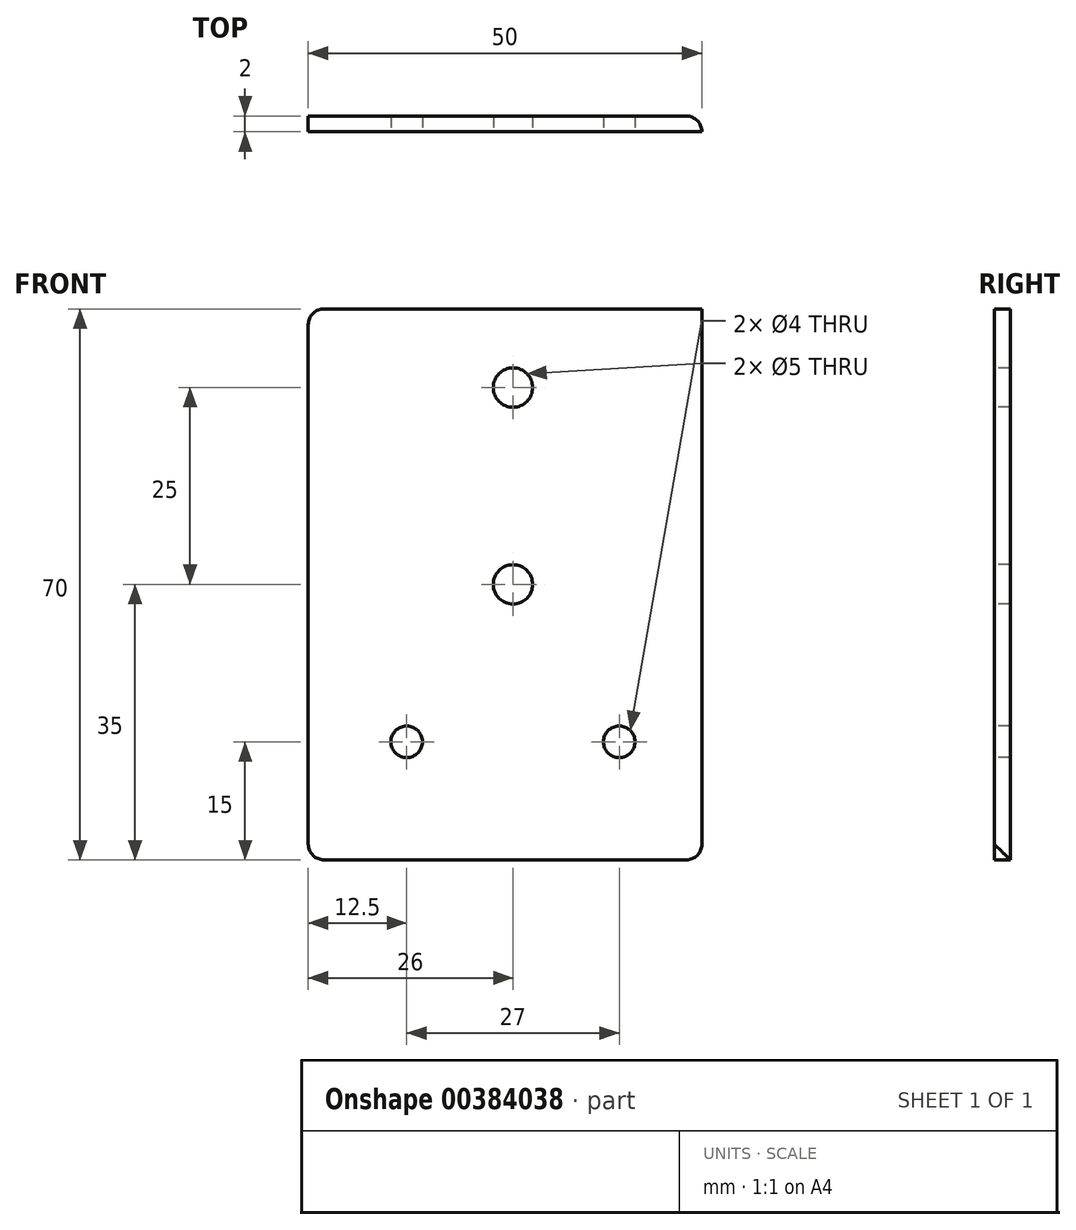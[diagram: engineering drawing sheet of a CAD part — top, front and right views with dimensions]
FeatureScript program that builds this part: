
annotation { "Feature Type Name" : "Feature", "Feature Type Description" : "" }
export const myFeature = defineFeature(function(context is Context, id is Id, definition is map)
    precondition{}
    {
        {
            var Q0;
            Q0=qCreatedBy(makeId("Front.planeOp"),FACE);
            var sketch = newSketch(context, id + "F0", { "sketchPlane" : qUnion([Q0])});
            skLineSegment(sketch, "E0.bottom", {"start": v(0, 0) * mm, "end": v(50, 0) * mm});
            skLineSegment(sketch, "E0.top", {"start": v(0, 70) * mm, "end": v(50, 70) * mm});
            skLineSegment(sketch, "E0.left", {"start": v(0, 0) * mm, "end": v(0, 70) * mm});
            skLineSegment(sketch, "E0.right", {"start": v(50, 0) * mm, "end": v(50, 70) * mm});
            skSolve(sketch);
        }
        {
            var Q0;
            Q0 = qSketchRegion(id + "F0", true);
            extrude(context, id + "F1", {"entities" : qUnion([Q0]), "depth" : 2 * mm});
        }
        {
            var Q0;
            Q0=makeQuery(id+"F1.opExtrude","SWEPT_EDGE",EDGE,{"disambiguationData":[OSD([sQuery(id+"F0.wireOp",EDGE,"E0.bottom"),sQuery(id+"F0.wireOp",EDGE,"E0.left")])]});
            var Q1;
            Q1=makeQuery(id+"F1.opExtrude","SWEPT_EDGE",EDGE,{"disambiguationData":[OSD([sQuery(id+"F0.wireOp",EDGE,"E0.bottom"),sQuery(id+"F0.wireOp",EDGE,"E0.right")])]});
            var Q2;
            Q2=makeQuery(id+"F1.opExtrude","CAP_EDGE",EDGE,{"disambiguationData":[OSD([sQuery(id+"F0.wireOp",EDGE,"E0.right")])],"isStart":true});
            var Q3;
            Q3=makeQuery(id+"F1.opExtrude","SWEPT_EDGE",EDGE,{"disambiguationData":[OSD([sQuery(id+"F0.wireOp",EDGE,"E0.top"),sQuery(id+"F0.wireOp",EDGE,"E0.left")])]});
            fillet(context, id + "F2", {"entities" : qUnion([Q0, Q1, Q2, Q3]), "radius" : 2 * mm, "tangentPropagation" : true, "allowEdgeOverflow" : false});
        }
        {
            var Q0;
            Q0=makeQuery(id+"F1.opExtrude","CAP_FACE",FACE,{"disambiguationData":[OSD([sQuery(id+"F0.wireOp",EDGE,"E0.bottom"),sQuery(id+"F0.wireOp",EDGE,"E0.top"),sQuery(id+"F0.wireOp",EDGE,"E0.left"),sQuery(id+"F0.wireOp",EDGE,"E0.right")])],"isStart":false});
            var sketch = newSketch(context, id + "F3", { "sketchPlane" : qUnion([Q0])});
            skLineSegment(sketch, "E1", {"start": v(26, 70) * mm, "end": v(26, 0) * mm, "construction": true});
            skLineSegment(sketch, "E2", {"start": v(0, 15) * mm, "end": v(50, 15) * mm, "construction": true});
            skCircle(sketch, "E3", {"center": v(12.5, 15) * mm, "radius": 2 * mm});
            skCircle(sketch, "E4", {"center": v(39.5, 15) * mm, "radius": 2 * mm});
            skCircle(sketch, "E5", {"center": v(26, 60) * mm, "radius": 2.5 * mm});
            skCircle(sketch, "E6", {"center": v(26, 35) * mm, "radius": 2.5 * mm});
            skSolve(sketch);
        }
        {
            var Q0;
            Q0 = qSketchRegion(id + "F3", true);
            extrude(context, id + "F4", {"entities" : qUnion([Q0]), "operationType" : NewBodyOperationType.REMOVE, "endBound" : BoundingType.THROUGH_ALL, "oppositeDirection" : true, "depth" : 25 * mm});
        }
    });
